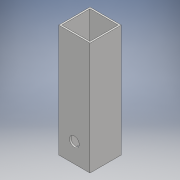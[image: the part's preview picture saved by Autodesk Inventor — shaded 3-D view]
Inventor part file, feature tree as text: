
AUTODESK INVENTOR PART (.ipt)
format: ipt  version: 2018 (Build 220112000, 112)  size: 111,104 bytes
history: native  units: mm
features: sketch x3, other x2, extrude x1, hole x1
ambient origin geometry x8: Origin, YZ Plane, XZ Plane, XY Plane, X Axis, Y Axis, Z Axis, Center Point
bodies: Body1 (feature_tree)
feature tree (7):
  other  "ソリッド1"
  sketch  "スケッチ1"
  other  "作業平面1"
  extrude  "押し出し1"  Depth=16.0mm
  hole  "穴1"  [1 undecoded]
  sketch  "スケッチ2"
  sketch  "スケッチ3"
note: 1 required parameter value undecoded (feature->parameter linkage not recoverable at this tier; creation-order binding heuristic only, values carry confidence <= 0.55)
